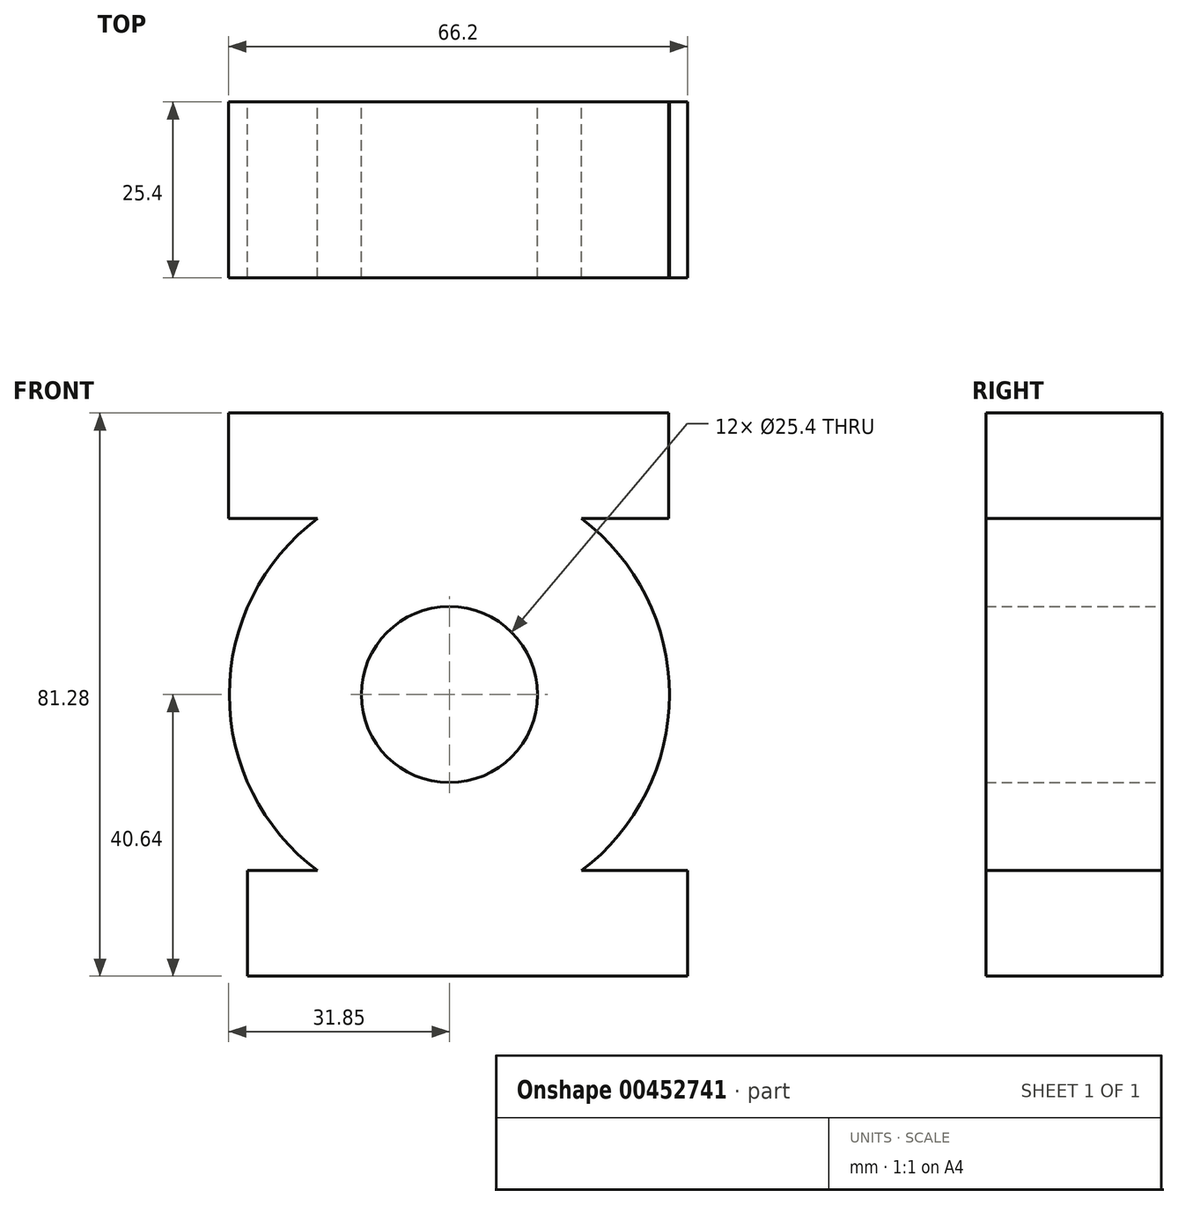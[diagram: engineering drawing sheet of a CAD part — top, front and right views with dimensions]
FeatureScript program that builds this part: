
annotation { "Feature Type Name" : "Feature", "Feature Type Description" : "" }
export const myFeature = defineFeature(function(context is Context, id is Id, definition is map)
    precondition{}
    {
        {
            var Q0;
            Q0=qCreatedBy(makeId("Front.planeOp"),FACE);
            var sketch = newSketch(context, id + "F0", { "sketchPlane" : qUnion([Q0])});
            skArc(sketch, "E0", {"start": v(-19.05, 25.4) * mm, "mid": v(-31.75, 0) * mm, "end": v(-19.05, -25.4) * mm});
            skCircle(sketch, "E1", {"center": v(0, 0) * mm, "radius": 12.7 * mm});
            skLineSegment(sketch, "E2.bottom", {"start": v(-31.85, 40.64) * mm, "end": v(31.65, 40.64) * mm});
            skLineSegment(sketch, "E2.top", {"start": v(-31.85, 25.4) * mm, "end": v(-19.05, 25.4) * mm});
            skLineSegment(sketch, "E2.left", {"start": v(-31.85, 40.64) * mm, "end": v(-31.85, 25.4) * mm});
            skLineSegment(sketch, "E2.right", {"start": v(31.65, 40.64) * mm, "end": v(31.65, 25.4) * mm});
            skLineSegment(sketch, "E3.bottom", {"start": v(-29.15, -25.4) * mm, "end": v(-19.05, -25.4) * mm});
            skLineSegment(sketch, "E3.top", {"start": v(-29.15, -40.64) * mm, "end": v(34.35, -40.64) * mm});
            skLineSegment(sketch, "E3.left", {"start": v(-29.15, -25.4) * mm, "end": v(-29.15, -40.64) * mm});
            skLineSegment(sketch, "E3.right", {"start": v(34.35, -25.4) * mm, "end": v(34.35, -40.64) * mm});
            skLineSegment(sketch, "E4.trimOffspring", {"start": v(19.05, 25.4) * mm, "end": v(31.65, 25.4) * mm});
            skArc(sketch, "E5.trimOffspring", {"start": v(19.05, -25.4) * mm, "mid": v(31.75, 0) * mm, "end": v(19.05, 25.4) * mm});
            skLineSegment(sketch, "E6.trimOffspring", {"start": v(19.05, -25.4) * mm, "end": v(34.35, -25.4) * mm});
            skSolve(sketch);
        }
        {
            var Q0;
            Q0=makeQuery(id+"F0.imprint","IMPRINT",FACE,{"disambiguationData":[TD([[makeQuery(id+"F0.imprint","IMPRINT",EDGE,{"derivedFrom":sQuery(id+"F0.wireOp",EDGE,"E0")}),1.0]])]});
            extrude(context, id + "F1", {"entities" : qUnion([Q0]), "depth" : 25.4 * mm});
        }
    });
